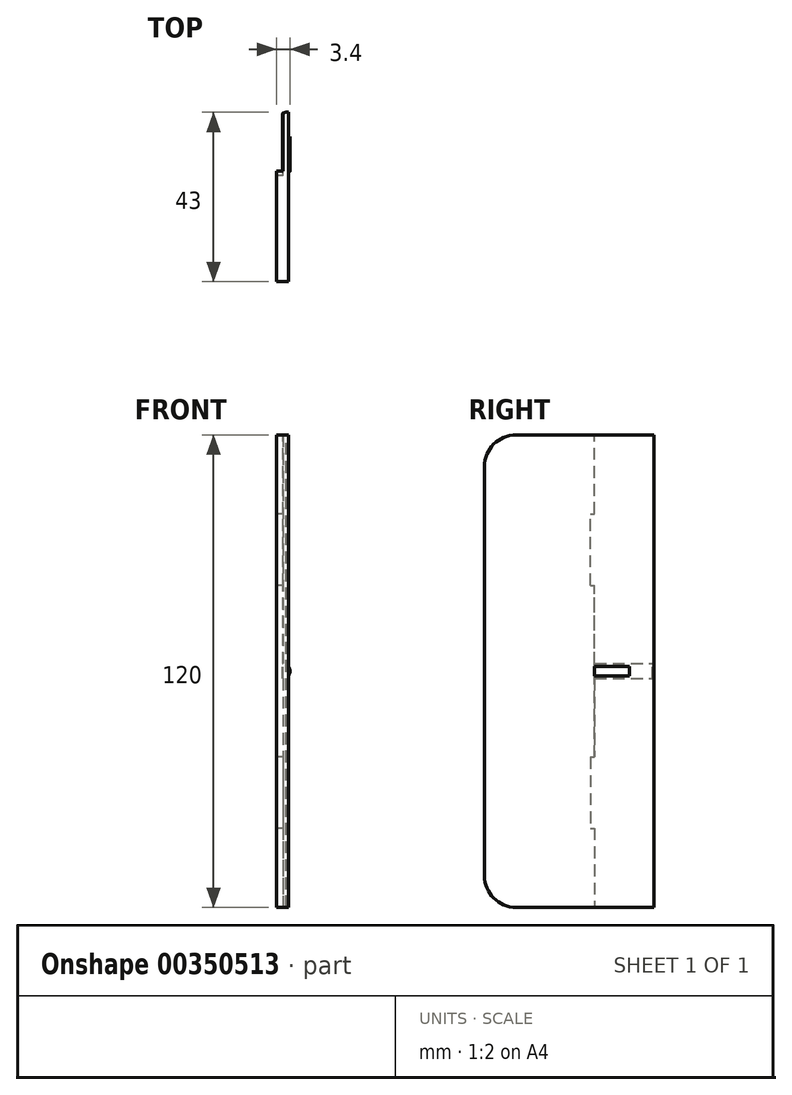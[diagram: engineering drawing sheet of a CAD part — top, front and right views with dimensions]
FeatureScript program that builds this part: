
annotation { "Feature Type Name" : "Feature", "Feature Type Description" : "" }
export const myFeature = defineFeature(function(context is Context, id is Id, definition is map)
    precondition{}
    {
        {
            var Q0;
            Q0=qCreatedBy(makeId("Top.planeOp"),FACE);
            var sketch = newSketch(context, id + "F0", { "sketchPlane" : qUnion([Q0])});
            skLineSegment(sketch, "E0.bottom", {"start": v(-1.5, 15) * mm, "end": v(1.5, 15) * mm});
            skLineSegment(sketch, "E0.top", {"start": v(-1.5, -15) * mm, "end": v(1.5, -15) * mm});
            skLineSegment(sketch, "E0.left", {"start": v(-1.5, 15) * mm, "end": v(-1.5, -15) * mm});
            skLineSegment(sketch, "E0.right", {"start": v(1.5, 15) * mm, "end": v(1.5, -15) * mm});
            skPoint(sketch, "E0.middle", {"position": v(0, 0) * mm});
            skSolve(sketch);
        }
        {
            var Q0;
            Q0=makeQuery(id+"F0.imprint","IMPRINT",FACE,{"disambiguationData":[TD([[makeQuery(id+"F0.imprint","IMPRINT",EDGE,{"derivedFrom":sQuery(id+"F0.wireOp",EDGE,"E0.bottom")}),-1.0]])]});
            extrude(context, id + "F1", {"entities" : qUnion([Q0]), "depth" : 70 * mm});
        }
        {
            var Q0;
            Q0=makeQuery(id+"F1.opExtrude","CAP_FACE",FACE,{"disambiguationData":[OSD([sQuery(id+"F0.wireOp",EDGE,"E0.bottom"),sQuery(id+"F0.wireOp",EDGE,"E0.top"),sQuery(id+"F0.wireOp",EDGE,"E0.left"),sQuery(id+"F0.wireOp",EDGE,"E0.right")])],"isStart":false});
            var sketch = newSketch(context, id + "F2", { "sketchPlane" : qUnion([Q0])});
            skLineSegment(sketch, "E1.bottom", {"start": v(-1.5, 15) * mm, "end": v(0, 15) * mm});
            skLineSegment(sketch, "E1.top", {"start": v(-1.5, 0) * mm, "end": v(0, 0) * mm});
            skLineSegment(sketch, "E1.left", {"start": v(-1.5, 15) * mm, "end": v(-1.5, 0) * mm});
            skLineSegment(sketch, "E1.right", {"start": v(0, 15) * mm, "end": v(0, 0) * mm});
            skSolve(sketch);
        }
        {
            var Q0;
            Q0=makeQuery(id+"F2.imprint","IMPRINT",FACE,{"disambiguationData":[TD([[makeQuery(id+"F2.imprint","IMPRINT",EDGE,{"derivedFrom":sQuery(id+"F2.wireOp",EDGE,"E1.bottom")}),-1.0]])]});
            extrude(context, id + "F3", {"entities" : qUnion([Q0]), "operationType" : NewBodyOperationType.REMOVE, "oppositeDirection" : true, "depth" : 70 * mm});
        }
        {
            var Q0;
            Q0=makeQuery(id+"F3.boolean.opBoolean","COPY",FACE,{"derivedFrom":makeQuery(id+"F3.opExtrude","SWEPT_FACE",FACE,{"disambiguationData":[OSD([sQuery(id+"F2.wireOp",EDGE,"E1.top")])]})});
            var sketch = newSketch(context, id + "F4", { "sketchPlane" : qUnion([Q0])});
            skLineSegment(sketch, "E2", {"start": v(0, 0) * mm, "end": v(0, 35) * mm, "construction": true});
            skCircle(sketch, "E3", {"center": v(0, 35) * mm, "radius": 1.9 * mm});
            skSolve(sketch);
        }
        {
            var Q0;
            {var subQ0=sQuery(id+"F4.wireOp",EDGE,"E3");var subQ1=makeQuery(id+"F3.boolean.opBoolean","COPY",EDGE,{"derivedFrom":makeQuery(id+"F3.opExtrude","SWEPT_EDGE",EDGE,{"disambiguationData":[OSD([sQuery(id+"F2.wireOp",EDGE,"E1.top"),sQuery(id+"F2.wireOp",EDGE,"E1.right")])]})});var subQ2=makeQuery(id+"F4.imprint","INTERSECT",VERTEX,{"disambiguationData":[OD(0.0)],"derivedFrom":[subQ1,subQ0]});Q0=makeQuery(id+"F4.imprint","IMPRINT",FACE,{"disambiguationData":[TD([[makeQuery(id+"F4.imprint","IMPRINT",EDGE,{"disambiguationData":[TD([[subQ2,1.0]])],"derivedFrom":subQ0}),1.0]])]});}
            extrude(context, id + "F5", {"entities" : qUnion([Q0]), "operationType" : NewBodyOperationType.ADD, "depth" : 8.8 * mm});
        }
        {
            var Q0;
            Q0=makeQuery(id+"F1.opExtrude","CAP_FACE",FACE,{"disambiguationData":[OSD([sQuery(id+"F0.wireOp",EDGE,"E0.bottom"),sQuery(id+"F0.wireOp",EDGE,"E0.top"),sQuery(id+"F0.wireOp",EDGE,"E0.left"),sQuery(id+"F0.wireOp",EDGE,"E0.right")])],"isStart":true});
            extrude(context, id + "F6", {"entities" : qUnion([Q0]), "operationType" : NewBodyOperationType.ADD, "depth" : 25 * mm});
        }
        {
            var Q0;
            Q0=makeQuery(id+"F1.opExtrude","CAP_FACE",FACE,{"disambiguationData":[OSD([sQuery(id+"F0.wireOp",EDGE,"E0.bottom"),sQuery(id+"F0.wireOp",EDGE,"E0.top"),sQuery(id+"F0.wireOp",EDGE,"E0.left"),sQuery(id+"F0.wireOp",EDGE,"E0.right")])],"isStart":false});
            extrude(context, id + "F7", {"entities" : qUnion([Q0]), "operationType" : NewBodyOperationType.ADD, "depth" : 25 * mm});
        }
        {
            var Q0;
            {var subQ0=sQuery(id+"F0.wireOp",EDGE,"E0.top");Q0=makeQuery(id+"F7.boolean.opBoolean","MERGE",FACE,{"derivedFrom":[makeQuery(id+"F6.boolean.opBoolean","MERGE",FACE,{"derivedFrom":[makeQuery(id+"F1.opExtrude","SWEPT_FACE",FACE,{"disambiguationData":[OSD([subQ0])]}),makeQuery(id+"F6.opExtrude","SWEPT_FACE",FACE,{"disambiguationData":[OSD([subQ0])]})]}),makeQuery(id+"F7.opExtrude","SWEPT_FACE",FACE,{"disambiguationData":[OSD([subQ0])]})]});}
            extrude(context, id + "F8", {"entities" : qUnion([Q0]), "operationType" : NewBodyOperationType.ADD, "depth" : 13 * mm});
        }
        {
            var Q0;
            {var subQ0=sQuery(id+"F0.wireOp",EDGE,"E0.bottom");Q0=makeQuery(id+"F7.boolean.opBoolean","MERGE",FACE,{"derivedFrom":[makeQuery(id+"F6.boolean.opBoolean","MERGE",FACE,{"derivedFrom":[makeQuery(id+"F5.boolean.opBoolean","MERGE",FACE,{"derivedFrom":[makeQuery(id+"F1.opExtrude","SWEPT_FACE",FACE,{"disambiguationData":[OSD([subQ0])]}),makeQuery(id+"F5.opExtrude","CAP_FACE",FACE,{"disambiguationData":[OSD([sQuery(id+"F0.wireOp",EDGE,"E0.left"),sQuery(id+"F2.wireOp",EDGE,"E1.top"),sQuery(id+"F2.wireOp",EDGE,"E1.left"),sQuery(id+"F2.wireOp",EDGE,"E1.right"),sQuery(id+"F4.wireOp",EDGE,"E3")])],"isStart":false})]}),makeQuery(id+"F6.opExtrude","SWEPT_FACE",FACE,{"disambiguationData":[OSD([subQ0])]})]}),makeQuery(id+"F7.opExtrude","SWEPT_FACE",FACE,{"disambiguationData":[OSD([subQ0])]})]});}
            var sketch = newSketch(context, id + "F9", { "sketchPlane" : qUnion([Q0])});
            skLineSegment(sketch, "E4.bottom", {"start": v(0, 33.1) * mm, "end": v(-0.1, 33.1) * mm});
            skLineSegment(sketch, "E4.top", {"start": v(0, -25) * mm, "end": v(-0.1, -25) * mm});
            skLineSegment(sketch, "E4.left", {"start": v(0, 33.1) * mm, "end": v(0, -25) * mm});
            skLineSegment(sketch, "E4.right", {"start": v(-0.1, 33.1) * mm, "end": v(-0.1, -25) * mm});
            skLineSegment(sketch, "E5.bottom", {"start": v(0, 36.9) * mm, "end": v(-0.1, 36.9) * mm});
            skLineSegment(sketch, "E5.top", {"start": v(0, 95) * mm, "end": v(-0.1, 95) * mm});
            skLineSegment(sketch, "E5.left", {"start": v(0, 36.9) * mm, "end": v(0, 95) * mm});
            skLineSegment(sketch, "E5.right", {"start": v(-0.1, 36.9) * mm, "end": v(-0.1, 95) * mm});
            skSolve(sketch);
        }
        {
            var Q0;
            Q0=makeQuery(id+"F9.imprint","IMPRINT",FACE,{"disambiguationData":[TD([[makeQuery(id+"F9.imprint","IMPRINT",EDGE,{"derivedFrom":sQuery(id+"F9.wireOp",EDGE,"E5.bottom")}),-1.0]])]});
            var Q1;
            Q1=makeQuery(id+"F9.imprint","IMPRINT",FACE,{"disambiguationData":[TD([[makeQuery(id+"F9.imprint","IMPRINT",EDGE,{"derivedFrom":sQuery(id+"F9.wireOp",EDGE,"E4.bottom")}),1.0]])]});
            extrude(context, id + "F10", {"entities" : qUnion([Q0, Q1]), "operationType" : NewBodyOperationType.REMOVE, "oppositeDirection" : true, "depth" : 15 * mm});
        }
        {
            var Q0;
            {var subQ0=sQuery(id+"F0.wireOp",EDGE,"E0.top");Q0=makeQuery(id+"F8.boolean.opBoolean","MERGE",FACE,{"derivedFrom":[makeQuery(id+"F6.opExtrude","CAP_FACE",FACE,{"disambiguationData":[OSD([sQuery(id+"F0.wireOp",EDGE,"E0.bottom"),subQ0,sQuery(id+"F0.wireOp",EDGE,"E0.left"),sQuery(id+"F0.wireOp",EDGE,"E0.right")])],"isStart":false}),makeQuery(id+"F8.opExtrude","SWEPT_FACE",FACE,{"disambiguationData":[OSD([subQ0]),TDD([makeQuery(id+"F6.opExtrude","CAP_EDGE",EDGE,{"disambiguationData":[OSD([subQ0])],"isStart":false})])]})]});}
            var sketch = newSketch(context, id + "F11", { "sketchPlane" : qUnion([Q0])});
            skLineSegment(sketch, "E6.bottom", {"start": v(0.1, -15) * mm, "end": v(0.3, -15) * mm, "construction": true});
            skLineSegment(sketch, "E6.top", {"start": v(0.1, -14.8) * mm, "end": v(0.3, -14.8) * mm, "construction": true});
            skLineSegment(sketch, "E6.left", {"start": v(0.1, -15) * mm, "end": v(0.1, -14.8) * mm, "construction": true});
            skLineSegment(sketch, "E6.right", {"start": v(0.3, -15) * mm, "end": v(0.3, -14.8) * mm, "construction": true});
            skLineSegment(sketch, "E7", {"start": v(0.3, -15) * mm, "end": v(-1.63, -13.07) * mm});
            skLineSegment(sketch, "E8", {"start": v(-1.63, -13.07) * mm, "end": v(-1.73, -15.35) * mm});
            skLineSegment(sketch, "E9", {"start": v(-1.73, -15.35) * mm, "end": v(0.3, -15) * mm});
            skSolve(sketch);
        }
        {
            var Q0;
            {var subQ1=sQuery(id+"F11.wireOp",EDGE,"E8");Q0=makeQuery(id+"F11.imprint","IMPRINT",FACE,{"disambiguationData":[TD([[makeQuery(id+"F11.imprint","IMPRINT",EDGE,{"derivedFrom":subQ1}),1.0]])]});}
            extrude(context, id + "F12", {"entities" : qUnion([Q0]), "operationType" : NewBodyOperationType.REMOVE, "oppositeDirection" : true, "depth" : 130 * mm});
        }
        {
            var Q0;
            {var subQ0=sQuery(id+"F0.wireOp",EDGE,"E0.top");Q0=makeQuery(id+"F8.boolean.opBoolean","MERGE",FACE,{"derivedFrom":[makeQuery(id+"F6.opExtrude","CAP_FACE",FACE,{"disambiguationData":[OSD([sQuery(id+"F0.wireOp",EDGE,"E0.bottom"),subQ0,sQuery(id+"F0.wireOp",EDGE,"E0.left"),sQuery(id+"F0.wireOp",EDGE,"E0.right")])],"isStart":false}),makeQuery(id+"F8.opExtrude","SWEPT_FACE",FACE,{"disambiguationData":[OSD([subQ0]),TDD([makeQuery(id+"F6.opExtrude","CAP_EDGE",EDGE,{"disambiguationData":[OSD([subQ0])],"isStart":false})])]})]});}
            var sketch = newSketch(context, id + "F13", { "sketchPlane" : qUnion([Q0])});
            skLineSegment(sketch, "E10", {"start": v(0.07, -14.78) * mm, "end": v(1, -15.05) * mm});
            skLineSegment(sketch, "E11", {"start": v(1, -15.05) * mm, "end": v(0.65, -15.27) * mm});
            skLineSegment(sketch, "E12", {"start": v(0.65, -15.27) * mm, "end": v(-0.27, -15.17) * mm});
            skLineSegment(sketch, "E13", {"start": v(0.07, -14.78) * mm, "end": v(-0.27, -15.17) * mm});
            skSolve(sketch);
        }
        {
            var Q0;
            {var subQ0=sQuery(id+"F13.wireOp",EDGE,"E11");Q0=makeQuery(id+"F13.imprint","IMPRINT",FACE,{"disambiguationData":[TD([[makeQuery(id+"F13.imprint","IMPRINT",EDGE,{"derivedFrom":subQ0}),-1.0]])]});}
            var Q1;
            {var subQ0=sQuery(id+"F13.wireOp",EDGE,"E10");var subQ1=sQuery(id+"F0.wireOp",EDGE,"E0.bottom");var subQ4=makeQuery(id+"F6.opExtrude","CAP_EDGE",EDGE,{"disambiguationData":[OSD([subQ1])],"isStart":false});var subQ5=makeQuery(id+"F13.imprint","INTERSECT",VERTEX,{"derivedFrom":[subQ4,subQ0]});Q1=makeQuery(id+"F13.imprint","IMPRINT",FACE,{"disambiguationData":[TD([[makeQuery(id+"F13.imprint","IMPRINT",EDGE,{"disambiguationData":[TD([[subQ5,1.0]])],"derivedFrom":subQ0}),-1.0]])]});}
            extrude(context, id + "F14", {"entities" : qUnion([Q0, Q1]), "operationType" : NewBodyOperationType.REMOVE, "oppositeDirection" : true, "depth" : 130 * mm});
        }
        {
            var Q0;
            {var subQ0=sQuery(id+"F0.wireOp",EDGE,"E0.top");Q0=makeQuery(id+"F8.opExtrude","CAP_EDGE",EDGE,{"disambiguationData":[OSD([subQ0]),TDD([makeQuery(id+"F7.opExtrude","CAP_EDGE",EDGE,{"disambiguationData":[OSD([subQ0])],"isStart":false})])],"isStart":false});}
            var Q1;
            {var subQ0=sQuery(id+"F0.wireOp",EDGE,"E0.top");Q1=makeQuery(id+"F8.opExtrude","CAP_EDGE",EDGE,{"disambiguationData":[OSD([subQ0]),TDD([makeQuery(id+"F6.opExtrude","CAP_EDGE",EDGE,{"disambiguationData":[OSD([subQ0])],"isStart":false})])],"isStart":false});}
            fillet(context, id + "F15", {"entities" : qUnion([Q0, Q1]), "radius" : 8 * mm, "tangentPropagation" : true, "allowEdgeOverflow" : false});
        }
        {
            var Q0;
            {var subQ0=sQuery(id+"F2.wireOp",EDGE,"E1.top");var subQ1=sQuery(id+"F2.wireOp",EDGE,"E1.right");var subQ2=sQuery(id+"F4.wireOp",EDGE,"E3");Q0=makeQuery(id+"F10.boolean.opBoolean","MERGE",FACE,{"derivedFrom":[makeQuery(id+"F7.boolean.opBoolean","MERGE",FACE,{"derivedFrom":[makeQuery(id+"F5.boolean.opBoolean","SPLIT",FACE,{"disambiguationData":[TD([makeQuery(id+"F5.opExtrude","SWEPT_FACE",FACE,{"disambiguationData":[OSD([subQ2]),TDD([makeQuery(id+"F4.imprint","IMPRINT",EDGE,{"disambiguationData":[TD([[makeQuery(id+"F4.imprint","INTERSECT",VERTEX,{"disambiguationData":[OD(0.0)],"derivedFrom":[makeQuery(id+"F3.boolean.opBoolean","COPY",EDGE,{"derivedFrom":makeQuery(id+"F3.opExtrude","SWEPT_EDGE",EDGE,{"disambiguationData":[OSD([subQ0,subQ1])]})}),subQ2]}),1.0]])],"derivedFrom":subQ2})])]})])],"derivedFrom":makeQuery(id+"F3.boolean.opBoolean","COPY",FACE,{"derivedFrom":makeQuery(id+"F3.opExtrude","SWEPT_FACE",FACE,{"disambiguationData":[OSD([subQ0])]})})}),makeQuery(id+"F7.opExtrude","SWEPT_FACE",FACE,{"disambiguationData":[OSD([subQ0])]})]}),makeQuery(id+"F10.opExtrude","CAP_FACE",FACE,{"disambiguationData":[OSD([sQuery(id+"F9.wireOp",EDGE,"E5.bottom"),sQuery(id+"F9.wireOp",EDGE,"E5.top"),sQuery(id+"F9.wireOp",EDGE,"E5.left"),sQuery(id+"F9.wireOp",EDGE,"E5.right")])],"isStart":false})]});}
            var sketch = newSketch(context, id + "F16", { "sketchPlane" : qUnion([Q0])});
            skLineSegment(sketch, "E14", {"start": v(0.7, 95) * mm, "end": v(0.7, 36.77) * mm, "construction": true});
            skLineSegment(sketch, "E15.bottom", {"start": v(-0.1, 74.93) * mm, "end": v(1.5, 74.93) * mm});
            skLineSegment(sketch, "E15.top", {"start": v(-0.1, 56.83) * mm, "end": v(1.5, 56.83) * mm});
            skLineSegment(sketch, "E15.left", {"start": v(-0.1, 74.93) * mm, "end": v(-0.1, 56.83) * mm});
            skLineSegment(sketch, "E15.right", {"start": v(1.5, 74.93) * mm, "end": v(1.5, 56.83) * mm});
            skPoint(sketch, "E15.middle", {"position": v(0.7, 65.88) * mm});
            skSolve(sketch);
        }
        {
            var Q0;
            {var subQ0=sQuery(id+"F2.wireOp",EDGE,"E1.top");var subQ1=sQuery(id+"F4.wireOp",EDGE,"E3");var subQ2=sQuery(id+"F2.wireOp",EDGE,"E1.right");Q0=makeQuery(id+"F10.boolean.opBoolean","MERGE",FACE,{"derivedFrom":[makeQuery(id+"F6.boolean.opBoolean","MERGE",FACE,{"derivedFrom":[makeQuery(id+"F5.boolean.opBoolean","SPLIT",FACE,{"disambiguationData":[TD([makeQuery(id+"F5.opExtrude","SWEPT_FACE",FACE,{"disambiguationData":[OSD([subQ1]),TDD([makeQuery(id+"F4.imprint","IMPRINT",EDGE,{"disambiguationData":[TD([[makeQuery(id+"F4.imprint","INTERSECT",VERTEX,{"disambiguationData":[OD(1.0)],"derivedFrom":[makeQuery(id+"F3.boolean.opBoolean","COPY",EDGE,{"derivedFrom":makeQuery(id+"F3.opExtrude","SWEPT_EDGE",EDGE,{"disambiguationData":[OSD([subQ0,subQ2])]})}),subQ1]}),-1.0]])],"derivedFrom":subQ1})])]})])],"derivedFrom":makeQuery(id+"F3.boolean.opBoolean","COPY",FACE,{"derivedFrom":makeQuery(id+"F3.opExtrude","SWEPT_FACE",FACE,{"disambiguationData":[OSD([subQ0])]})})}),makeQuery(id+"F6.opExtrude","SWEPT_FACE",FACE,{"disambiguationData":[OSD([subQ0])]})]}),makeQuery(id+"F10.opExtrude","CAP_FACE",FACE,{"disambiguationData":[OSD([sQuery(id+"F9.wireOp",EDGE,"E4.bottom"),sQuery(id+"F9.wireOp",EDGE,"E4.top"),sQuery(id+"F9.wireOp",EDGE,"E4.left"),sQuery(id+"F9.wireOp",EDGE,"E4.right")])],"isStart":false})]});}
            var sketch = newSketch(context, id + "F17", { "sketchPlane" : qUnion([Q0])});
            skLineSegment(sketch, "E16", {"start": v(0.7, -25) * mm, "end": v(0.7, 33.23) * mm, "construction": true});
            skLineSegment(sketch, "E17.bottom", {"start": v(-0.1, 13.17) * mm, "end": v(1.5, 13.17) * mm});
            skLineSegment(sketch, "E17.top", {"start": v(-0.1, -4.93) * mm, "end": v(1.5, -4.93) * mm});
            skLineSegment(sketch, "E17.left", {"start": v(-0.1, 13.17) * mm, "end": v(-0.1, -4.93) * mm});
            skLineSegment(sketch, "E17.right", {"start": v(1.5, 13.17) * mm, "end": v(1.5, -4.93) * mm});
            skPoint(sketch, "E17.middle", {"position": v(0.7, 4.12) * mm});
            skSolve(sketch);
        }
        {
            var Q0;
            Q0=makeQuery(id+"F17.imprint","IMPRINT",FACE,{"disambiguationData":[TD([[makeQuery(id+"F17.imprint","IMPRINT",EDGE,{"derivedFrom":sQuery(id+"F17.wireOp",EDGE,"E17.bottom")}),-1.0]])]});
            var Q1;
            Q1=makeQuery(id+"F16.imprint","IMPRINT",FACE,{"disambiguationData":[TD([[makeQuery(id+"F16.imprint","IMPRINT",EDGE,{"derivedFrom":sQuery(id+"F16.wireOp",EDGE,"E15.bottom")}),-1.0]])]});
            extrude(context, id + "F18", {"entities" : qUnion([Q0, Q1]), "operationType" : NewBodyOperationType.REMOVE, "oppositeDirection" : true, "depth" : 1.1 * mm});
        }
        {
            var Q0;
            Q0=qCreatedBy(makeId("Top.planeOp"),FACE);
            var sketch = newSketch(context, id + "F19", { "sketchPlane" : qUnion([Q0])});
            skLineSegment(sketch, "E18", {"start": v(-2.37, 7.18) * mm, "end": v(0, 8.8) * mm});
            skLineSegment(sketch, "E19", {"start": v(0, 8.8) * mm, "end": v(-4.65, 10.02) * mm});
            skLineSegment(sketch, "E20", {"start": v(-4.65, 10.02) * mm, "end": v(-4.65, 8.36) * mm});
            skLineSegment(sketch, "E21", {"start": v(-4.65, 8.36) * mm, "end": v(-2.37, 7.18) * mm});
            skSolve(sketch);
        }
        {
            var Q0;
            Q0=makeQuery(id+"F19.imprint","IMPRINT",FACE,{"disambiguationData":[TD([[makeQuery(id+"F19.imprint","IMPRINT",EDGE,{"derivedFrom":sQuery(id+"F19.wireOp",EDGE,"E18")}),1.0]])]});
            extrude(context, id + "F20", {"entities" : qUnion([Q0]), "operationType" : NewBodyOperationType.REMOVE, "depth" : 44.7 * mm});
        }
    });
